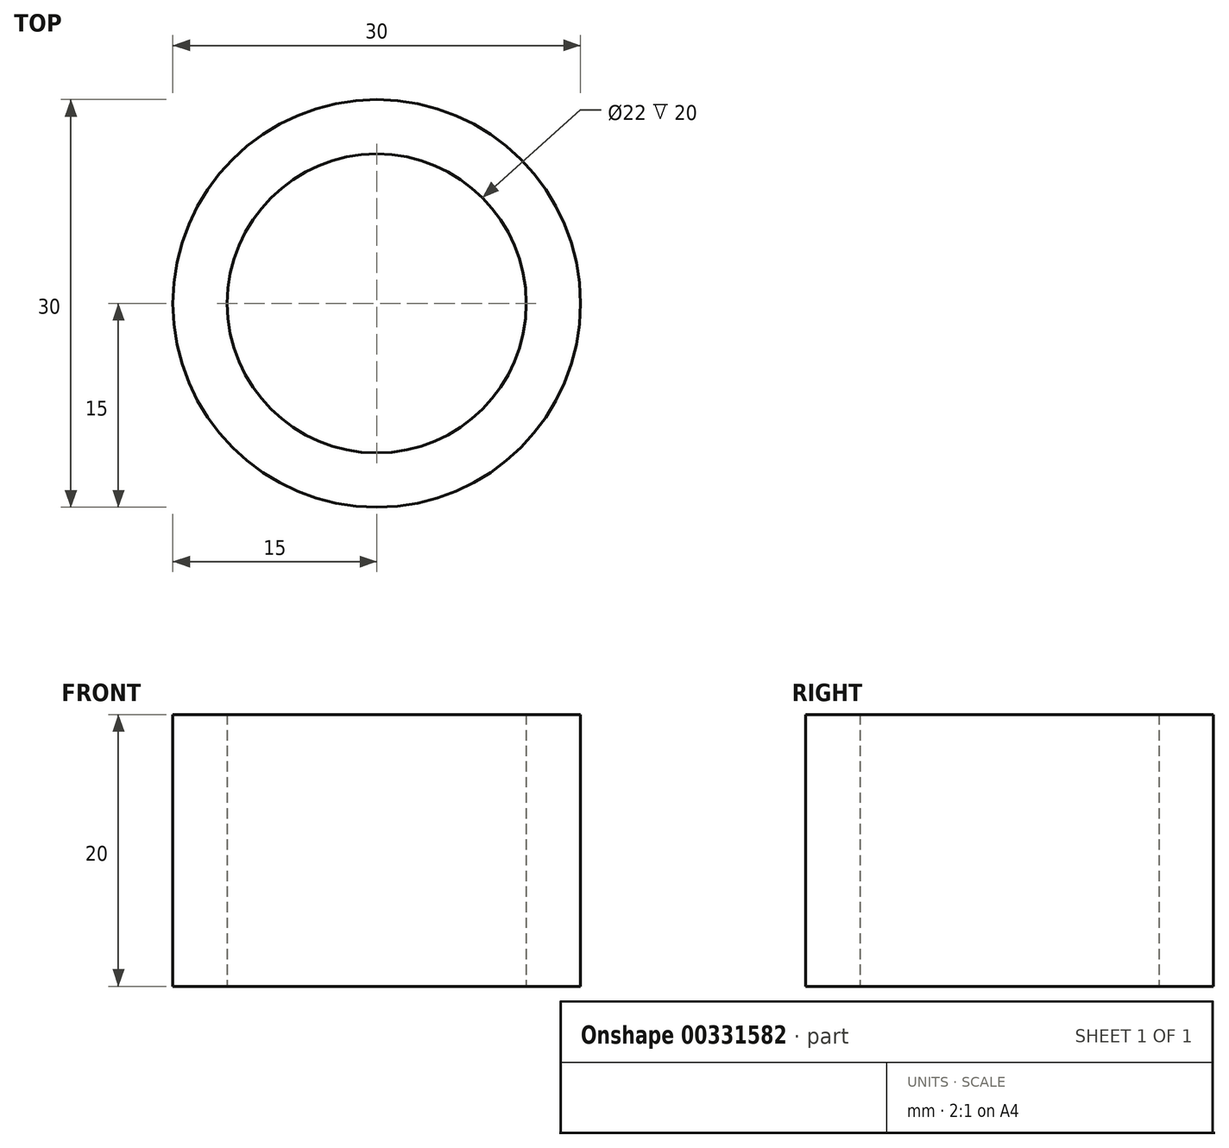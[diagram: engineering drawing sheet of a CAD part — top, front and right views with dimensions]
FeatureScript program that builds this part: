
annotation { "Feature Type Name" : "Feature", "Feature Type Description" : "" }
export const myFeature = defineFeature(function(context is Context, id is Id, definition is map)
    precondition{}
    {
        {
            var Q0;
            Q0=qCreatedBy(makeId("Top.planeOp"),FACE);
            var sketch = newSketch(context, id + "F0", { "sketchPlane" : qUnion([Q0])});
            skCircle(sketch, "E0", {"center": v(0, 0) * mm, "radius": 11 * mm});
            skCircle(sketch, "E1", {"center": v(0, 0) * mm, "radius": 15 * mm});
            skSolve(sketch);
        }
        {
            var Q0;
            Q0 = qSketchRegion(id + "F0", true);
            extrude(context, id + "F1", {"entities" : qUnion([Q0]), "depth" : 20 * mm});
        }
    });
